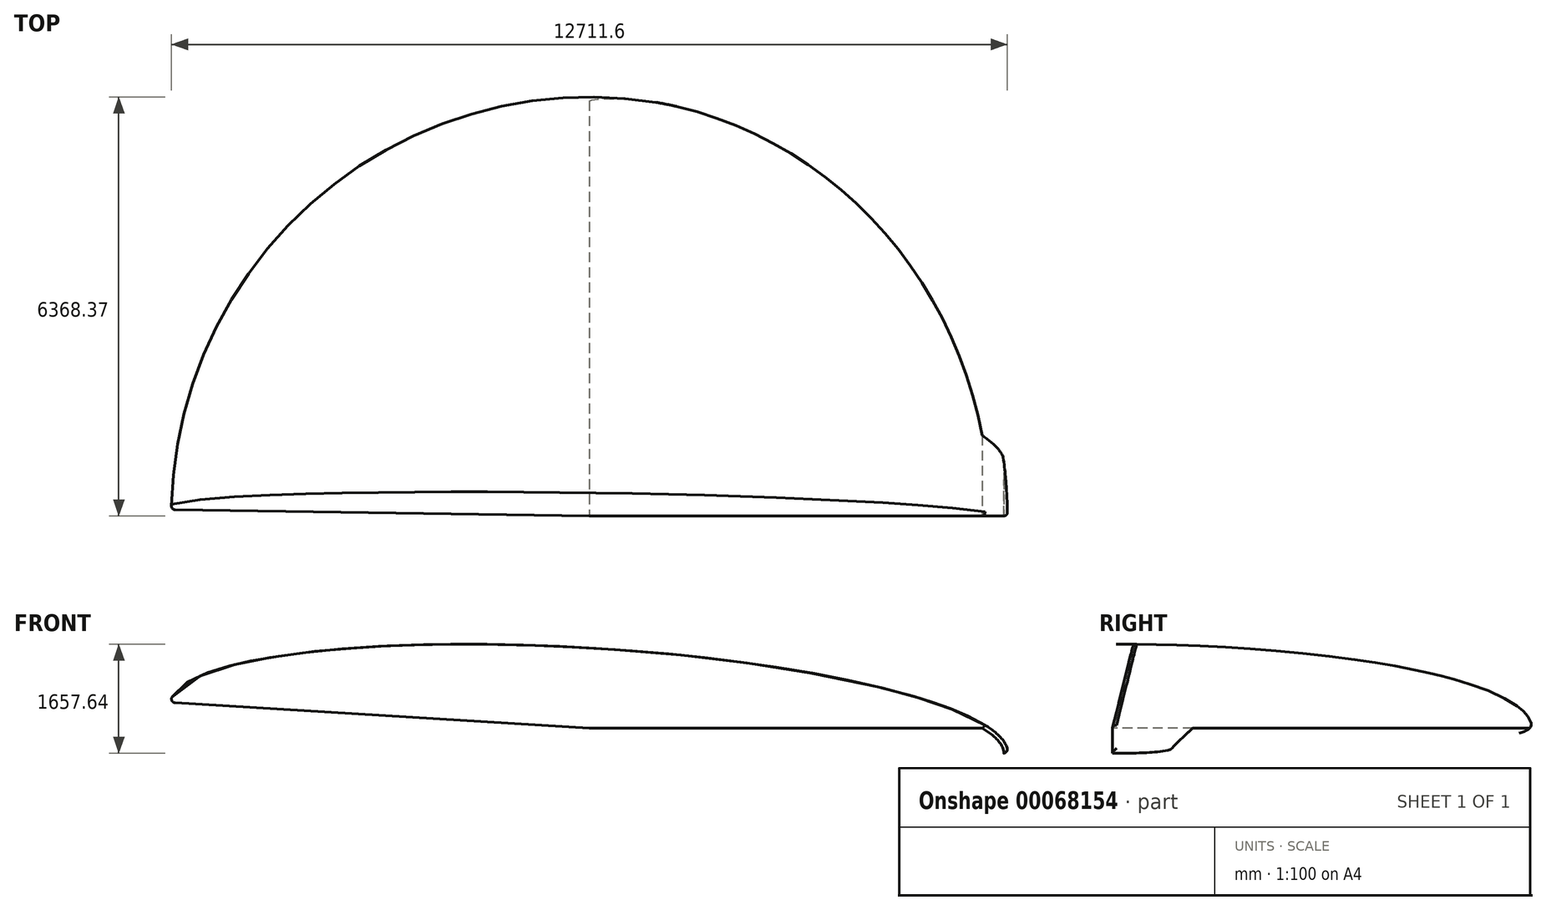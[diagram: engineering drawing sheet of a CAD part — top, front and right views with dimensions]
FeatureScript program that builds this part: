
annotation { "Feature Type Name" : "Feature", "Feature Type Description" : "" }
export const myFeature = defineFeature(function(context is Context, id is Id, definition is map)
    precondition{}
    {
        {
            var Q0;
            Q0=qCreatedBy(makeId("Front.planeOp"),FACE);
            var sketch = newSketch(context, id + "F0", { "sketchPlane" : qUnion([Q0])});
            skEllipticalArc(sketch, "E0", {});
            skLineSegment(sketch, "E1", {"start": v(2743.2, 0) * mm, "end": v(2743.2, 941.5) * mm, "construction": true});
            skLineSegment(sketch, "E2", {"start": v(0, 0) * mm, "end": v(2743.2, 0) * mm, "construction": true});
            skPoint(sketch, "E3.endSnap0", {"position": v(6367.31, -387.27) * mm});
            skLineSegment(sketch, "E4", {"start": v(0, 0) * mm, "end": v(6367.31, -387.27) * mm});
            skLineSegment(sketch, "E5", {"start": v(0, 0) * mm, "end": v(74.02, 1216.95) * mm});
            skLineSegment(sketch, "E6", {"start": v(0, 0) * mm, "end": v(137.15, 2254.93) * mm, "construction": true});
            const initialGuessF0  = {"E0": [0, 0, 0.9981554836332803, -0.06070939377734134, 6.37907874648794, 1.2192, 0, 1.5707963267948966]};
            skSetInitialGuess(sketch, initialGuessF0);
            skSolve(sketch);
        }
        {
            var Q0;
            Q0 = qSketchRegion(id + "F0", true);
            var Q1;
            Q1=sQuery(id+"F0.wireOp",EDGE,"E6");
            revolve(context, id + "F1", {"entities" : qUnion([Q0]), "axis" : qUnion([Q1]), "revolveType" : RevolveType.ONE_DIRECTION, "angle" : 180 * degree});
        }
        {
            var Q0;
            Q0=qCreatedBy(makeId("Right.planeOp"),FACE);
            var sketch = newSketch(context, id + "F2", { "sketchPlane" : qUnion([Q0])});
            skLineSegment(sketch, "E7", {"start": v(0, 0) * mm, "end": v(718.48, 2881.67) * mm});
            skLineSegment(sketch, "E8", {"start": v(718.48, 2881.67) * mm, "end": v(-350.87, 3148.3) * mm});
            skLineSegment(sketch, "E9", {"start": v(-350.87, 3148.3) * mm, "end": v(-1069.35, 266.62) * mm});
            skLineSegment(sketch, "E10", {"start": v(-1069.35, 266.62) * mm, "end": v(0, 0) * mm});
            skLineSegment(sketch, "E11", {"start": v(0, 0) * mm, "end": v(0, 2075.86) * mm, "construction": true});
            skSolve(sketch);
        }
        {
            var Q0;
            Q0 = qSketchRegion(id + "F2", true);
            extrude(context, id + "F3", {"entities" : qUnion([Q0]), "operationType" : NewBodyOperationType.REMOVE, "depth" : 24384 * mm, "hasSecondDirection" : true, "secondDirectionOppositeDirection" : true, "secondDirectionDepth" : 24384 * mm});
        }
        {
            var Q0;
            Q0=makeQuery(id+"F1.opRevolve","SWEPT_FACE",FACE,{"disambiguationData":[OSD([sQuery(id+"F0.wireOp",EDGE,"E0")])]});
            fillet(context, id + "F4", {"entities" : qUnion([Q0]), "radius" : 60.96 * mm, "tangentPropagation" : true, "allowEdgeOverflow" : false});
        }
        {
            var Q0;
            Q0=makeQuery(id+"F1.opRevolve","CAP_FACE",FACE,{"disambiguationData":[OSD([sQuery(id+"F0.wireOp",EDGE,"E0"),sQuery(id+"F0.wireOp",EDGE,"E4"),sQuery(id+"F0.wireOp",EDGE,"E5")])],"isStart":false});
            var sketch = newSketch(context, id + "F5", { "sketchPlane" : qUnion([Q0])});
            skSolve(sketch);
        }
        {
            var Q0;
            {var subQ0=sQuery(id+"F0.wireOp",EDGE,"E4");Q0=makeQuery(id+"F5.imprint","IMPRINT",FACE,{"disambiguationData":[TD([[makeQuery(id+"F5.imprint","IMPRINT",EDGE,{"derivedFrom":makeQuery(id+"F1.opRevolve","CAP_EDGE",EDGE,{"disambiguationData":[OSD([subQ0])],"isStart":false})}),-1.0]])]});}
            extrude(context, id + "F6", {"entities" : qUnion([Q0]), "operationType" : NewBodyOperationType.REMOVE, "oppositeDirection" : true, "depth" : 6498.35 * mm});
        }
    });
